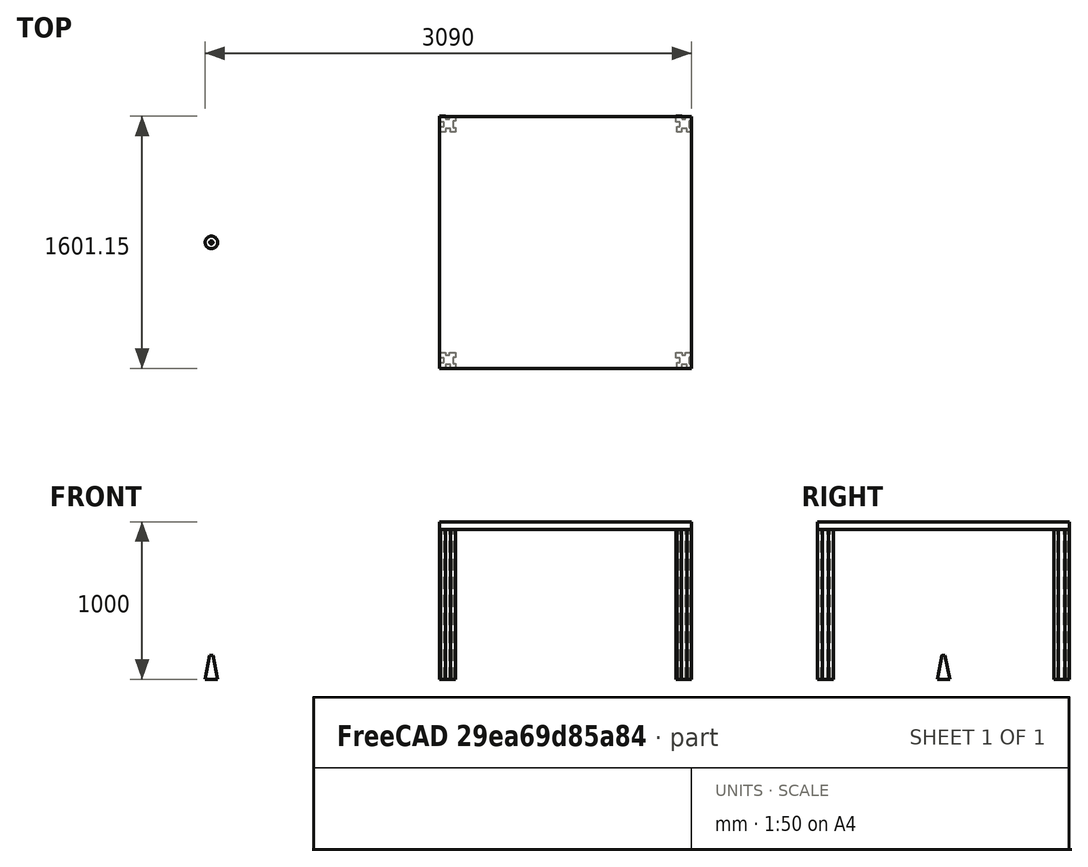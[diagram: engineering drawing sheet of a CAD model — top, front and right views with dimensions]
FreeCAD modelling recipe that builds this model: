
FCSTD DOCUMENT
Label: RobotExample
objects: PartDesign::Pad×5, Part::Plane×1, Part::Box×1, Sketcher::SketchObjectSF×1, Robot::TrajectoryObject×1, Robot::RobotObject×1, Part::Cone×1, App::DocumentObjectGroup×1
note: 9 computed .brp shape members not serialized (recipe doc carries the construction recipe); baked Part::Feature solids carry a one-line shape summary decoded from their .brp

FEATURE [Part::Plane] Plane
  Length = 10000
  Placement = pos=(-5000,-5000,0) rot=(0,0,1;0rad)
  Width = 10000
FEATURE [PartDesign::Pad] Pad  label="Bein1"
  Length = 100
  Placement = pos=(1500,-750,0) rot=(0,0,1;0rad)
FEATURE [PartDesign::Pad] Pad1  label="Bein2"
  Length = 100
  Placement = pos=(1500,750,0) rot=(0,0,1;0rad)
FEATURE [PartDesign::Pad] Pad2  label="Bein3"
  Length = 100
  Placement = pos=(3000,-750,0) rot=(0,0,1;0rad)
FEATURE [PartDesign::Pad] Pad3  label="Bein4"
  Length = 100
  Placement = pos=(3000,750,0) rot=(0,0,1;0rad)
FEATURE [Part::Box] Box  label="TischPlatte"
  Height = 50
  Length = 1600
  Placement = pos=(1450,-800,950) rot=(0,0,1;0rad)
  Width = 1600
FEATURE [Sketcher::SketchObjectSF] Sketch
FEATURE [PartDesign::Pad] Pad4  label="PartToWork"
  Length = 100
  Placement = pos=(2217.27,-81.4724,1513.01) rot=(0,0,1;0rad)
FEATURE [Robot::TrajectoryObject] Trajectory
FEATURE [Robot::RobotObject] Robot
  Axis1 = -5.76791e-12
  Axis2 = -90.0001
  Axis3 = 90
  Axis4 = 4.72328e-11
  Axis5 = 45.0001
  Axis6 = 2.9999
  Tcp = pos=(1737.13,-1.51113e-13,2187.87) rot=(-0.026175,0.999598,-0.010842;2.35648rad)
FEATURE [Part::Cone] Cone  label="ToolShape"
  Angle = 360
  Height = 150
  Radius1 = 40
  Radius2 = 10
FEATURE [App::DocumentObjectGroup] Gruppe  label="SetUp"
  Group = -> [Plane,Pad,Pad1,Pad2,Pad3,Box,Sketch,Cone]
